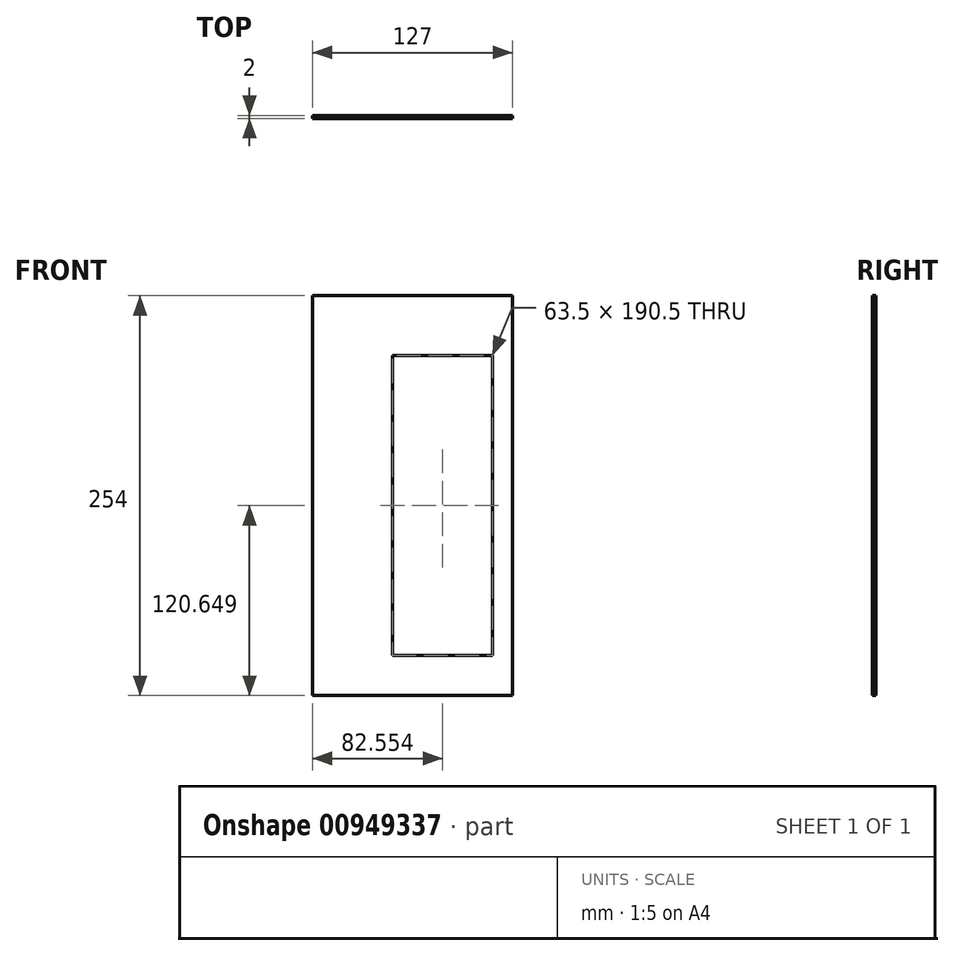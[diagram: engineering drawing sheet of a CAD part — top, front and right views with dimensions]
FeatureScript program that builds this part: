
annotation { "Feature Type Name" : "Feature", "Feature Type Description" : "" }
export const myFeature = defineFeature(function(context is Context, id is Id, definition is map)
    precondition{}
    {
        {
            var Q0;
            Q0=qCreatedBy(makeId("Front.planeOp"),FACE);
            var sketch = newSketch(context, id + "F0", { "sketchPlane" : qUnion([Q0])});
            skLineSegment(sketch, "E0.bottom", {"start": v(-69.15, 139.7) * mm, "end": v(57.85, 139.7) * mm});
            skLineSegment(sketch, "E0.top", {"start": v(-69.15, -114.3) * mm, "end": v(57.85, -114.3) * mm});
            skLineSegment(sketch, "E0.left", {"start": v(-69.15, 139.7) * mm, "end": v(-69.15, -114.3) * mm});
            skLineSegment(sketch, "E0.right", {"start": v(57.85, 139.7) * mm, "end": v(57.85, -114.3) * mm});
            skPoint(sketch, "E1", {"position": v(0, 0) * mm});
            skSolve(sketch);
        }
        {
            var Q0;
            Q0 = qSketchRegion(id + "F0", true);
            extrude(context, id + "F1", {"entities" : qUnion([Q0]), "depth" : 2 * mm, "offsetDistance" : 25.4 * mm});
        }
        {
            var Q0;
            Q0=makeQuery(id+"F1.opExtrude","CAP_FACE",FACE,{"disambiguationData":[OSD([sQuery(id+"F0.wireOp",EDGE,"E0.bottom"),sQuery(id+"F0.wireOp",EDGE,"E0.top"),sQuery(id+"F0.wireOp",EDGE,"E0.left"),sQuery(id+"F0.wireOp",EDGE,"E0.right")])],"isStart":false});
            var sketch = newSketch(context, id + "F2", { "sketchPlane" : qUnion([Q0])});
            skLineSegment(sketch, "E2.bottom", {"start": v(45.15, 101.6) * mm, "end": v(-18.35, 101.6) * mm});
            skLineSegment(sketch, "E2.top", {"start": v(45.15, -88.9) * mm, "end": v(-18.35, -88.9) * mm});
            skLineSegment(sketch, "E2.left", {"start": v(45.15, 101.6) * mm, "end": v(45.15, -88.9) * mm});
            skLineSegment(sketch, "E2.right", {"start": v(-18.35, 101.6) * mm, "end": v(-18.35, -88.9) * mm});
            skSolve(sketch);
        }
        {
            var Q0;
            Q0=makeQuery(id+"F2.imprint","IMPRINT",FACE,{"disambiguationData":[TD([[makeQuery(id+"F2.imprint","IMPRINT",EDGE,{"derivedFrom":sQuery(id+"F2.wireOp",EDGE,"E2.bottom")}),1.0]])]});
            extrude(context, id + "F3", {"entities" : qUnion([Q0]), "operationType" : NewBodyOperationType.REMOVE, "oppositeDirection" : true, "depth" : 25.4 * mm, "offsetDistance" : 25.4 * mm});
        }
    });
